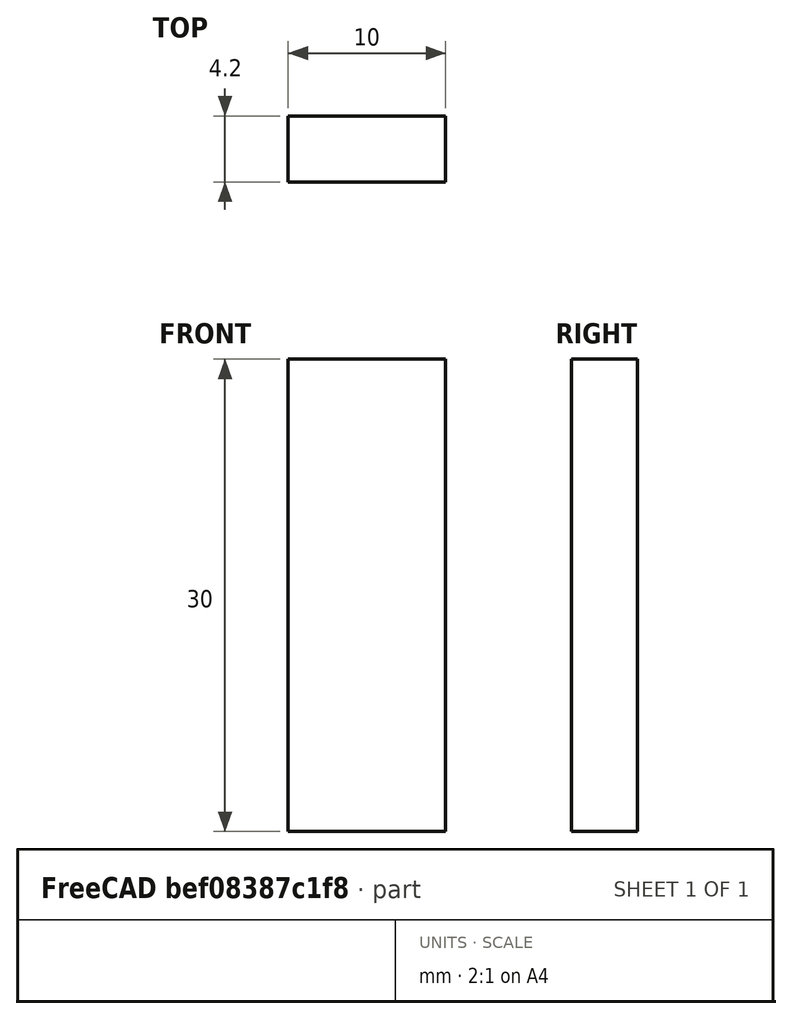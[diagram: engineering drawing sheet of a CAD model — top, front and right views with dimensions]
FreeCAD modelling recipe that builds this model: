
FCSTD DOCUMENT  (FreeCAD 0.18R4 (GitTag))
Label: liaison bras
License: All rights reserved
LicenseURL: http://en.wikipedia.org/wiki/All_rights_reserved
objects: Sketcher::SketchObject×1, PartDesign::Pad×1, PartDesign::Body×1
note: 4 computed .brp shape members not serialized (recipe doc carries the construction recipe); baked Part::Feature solids carry a one-line shape summary decoded from their .brp

FEATURE [Sketcher::SketchObject] Sketch
  MapMode = 5
  Support = -> [XY_Plane]
  sketch-geometry (4):
    g0: LineSegment StartX=-10 StartY=4.2 StartZ=0 EndX=0 EndY=4.2 EndZ=0
    g1: LineSegment StartX=0 StartY=4.2 StartZ=0 EndX=0 EndY=0 EndZ=0
    g2: LineSegment StartX=0 StartY=0 StartZ=0 EndX=-10 EndY=0 EndZ=0
    g3: LineSegment StartX=-10 StartY=0 StartZ=0 EndX=-10 EndY=4.2 EndZ=0
  constraints (11):
    c: Coincident(g0,g1)
    c: Coincident(g1,g2)
    c: Coincident(g2,g3)
    c: Coincident(g3,g0)
    c: Horizontal(g0)
    c: Horizontal(g2)
    c: Vertical(g1)
    c: Vertical(g3)
    c: DistanceX(g0,g0) = 10
    c: Coincident(g1,g-1)
    c: DistanceY(g1,g1) = 4.2
FEATURE [PartDesign::Pad] Pad
  Length = 30
  Length2 = 100
  Profile = -> Sketch
  Type = 0
FEATURE [PartDesign::Body] Body
  Group = -> [Sketch,Pad]
  Origin = -> Origin
  Tip = -> Pad
